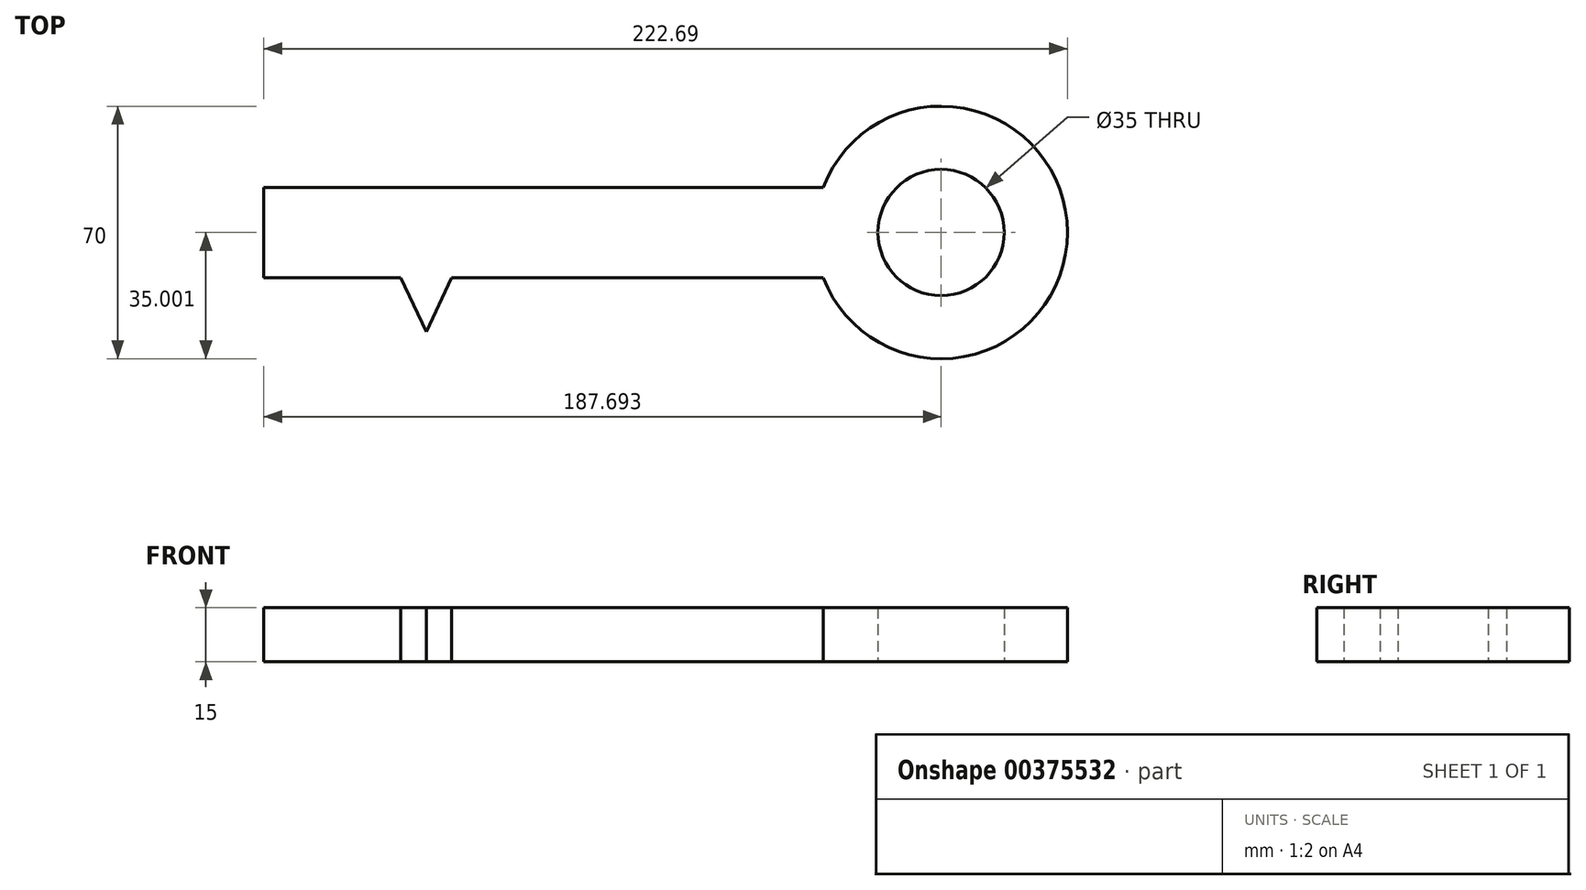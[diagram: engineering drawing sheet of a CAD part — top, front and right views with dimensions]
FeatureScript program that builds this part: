
annotation { "Feature Type Name" : "Feature", "Feature Type Description" : "" }
export const myFeature = defineFeature(function(context is Context, id is Id, definition is map)
    precondition{}
    {
        {
            var Q0;
            Q0=qCreatedBy(makeId("Top.planeOp"),FACE);
            var sketch = newSketch(context, id + "F0", { "sketchPlane" : qUnion([Q0])});
            skLineSegment(sketch, "E0.bottom", {"start": v(-61.76, -4.36) * mm, "end": v(93.24, -4.36) * mm});
            skLineSegment(sketch, "E0.top", {"start": v(-61.76, -29.36) * mm, "end": v(93.24, -29.36) * mm});
            skLineSegment(sketch, "E0.left", {"start": v(-61.76, -4.36) * mm, "end": v(-61.76, -29.36) * mm});
            skLineSegment(sketch, "E0.right", {"start": v(93.24, -4.36) * mm, "end": v(93.24, -29.36) * mm});
            skLineSegment(sketch, "E1.bottom", {"start": v(-61.76, -29.36) * mm, "end": v(-51.76, -29.36) * mm});
            skLineSegment(sketch, "E1.top", {"start": v(-61.76, -59.36) * mm, "end": v(-51.76, -59.36) * mm});
            skLineSegment(sketch, "E1.left", {"start": v(-61.76, -29.36) * mm, "end": v(-61.76, -59.36) * mm});
            skLineSegment(sketch, "E1.right", {"start": v(-51.76, -29.36) * mm, "end": v(-51.76, -59.36) * mm});
            skLineSegment(sketch, "E2.bottom", {"start": v(-41.76, -29.36) * mm, "end": v(-33.76, -29.36) * mm});
            skLineSegment(sketch, "E2.top", {"start": v(-41.76, -44.36) * mm, "end": v(-33.76, -44.36) * mm});
            skLineSegment(sketch, "E2.left", {"start": v(-41.76, -29.36) * mm, "end": v(-41.76, -44.36) * mm});
            skLineSegment(sketch, "E2.right", {"start": v(-33.76, -29.36) * mm, "end": v(-33.76, -44.36) * mm});
            skLineSegment(sketch, "E3", {"start": v(-23.76, -29.36) * mm, "end": v(-16.76, -44.36) * mm});
            skLineSegment(sketch, "E4", {"start": v(-16.76, -44.36) * mm, "end": v(-9.76, -29.36) * mm});
            skLineSegment(sketch, "E5", {"start": v(-23.76, -29.36) * mm, "end": v(-9.76, -29.36) * mm});
            skArc(sketch, "E6", {"start": v(93.24, -29.36) * mm, "mid": v(160.93, -16.86) * mm, "end": v(93.24, -4.36) * mm});
            skCircle(sketch, "E7", {"center": v(125.93, -16.86) * mm, "radius": 17.5 * mm});
            skSolve(sketch);
        }
        {
            var Q0;
            Q0=makeQuery(id+"F0.imprint","IMPRINT",FACE,{"disambiguationData":[TD([[makeQuery(id+"F0.imprint","IMPRINT",EDGE,{"derivedFrom":sQuery(id+"F0.wireOp",EDGE,"E1.bottom")}),-1.0]])]});
            var Q1;
            Q1=makeQuery(id+"F0.imprint","IMPRINT",FACE,{"disambiguationData":[TD([[makeQuery(id+"F0.imprint","IMPRINT",EDGE,{"derivedFrom":sQuery(id+"F0.wireOp",EDGE,"E2.bottom")}),-1.0]])]});
            var Q2;
            Q2=makeQuery(id+"F0.imprint","IMPRINT",FACE,{"disambiguationData":[TD([[makeQuery(id+"F0.imprint","IMPRINT",EDGE,{"derivedFrom":sQuery(id+"F0.wireOp",EDGE,"E3")}),1.0]])]});
            var Q3;
            Q3=makeQuery(id+"F0.imprint","IMPRINT",FACE,{"disambiguationData":[TD([[makeQuery(id+"F0.imprint","IMPRINT",EDGE,{"derivedFrom":sQuery(id+"F0.wireOp",EDGE,"E0.bottom")}),-1.0]])]});
            var Q4;
            Q4=makeQuery(id+"F0.imprint","IMPRINT",FACE,{"disambiguationData":[TD([[makeQuery(id+"F0.imprint","IMPRINT",EDGE,{"derivedFrom":sQuery(id+"F0.wireOp",EDGE,"E0.right")}),1.0]])]});
            extrude(context, id + "F1", {"entities" : qUnion([Q0, Q1, Q2, Q3, Q4]), "depth" : 15 * mm});
        }
    });
